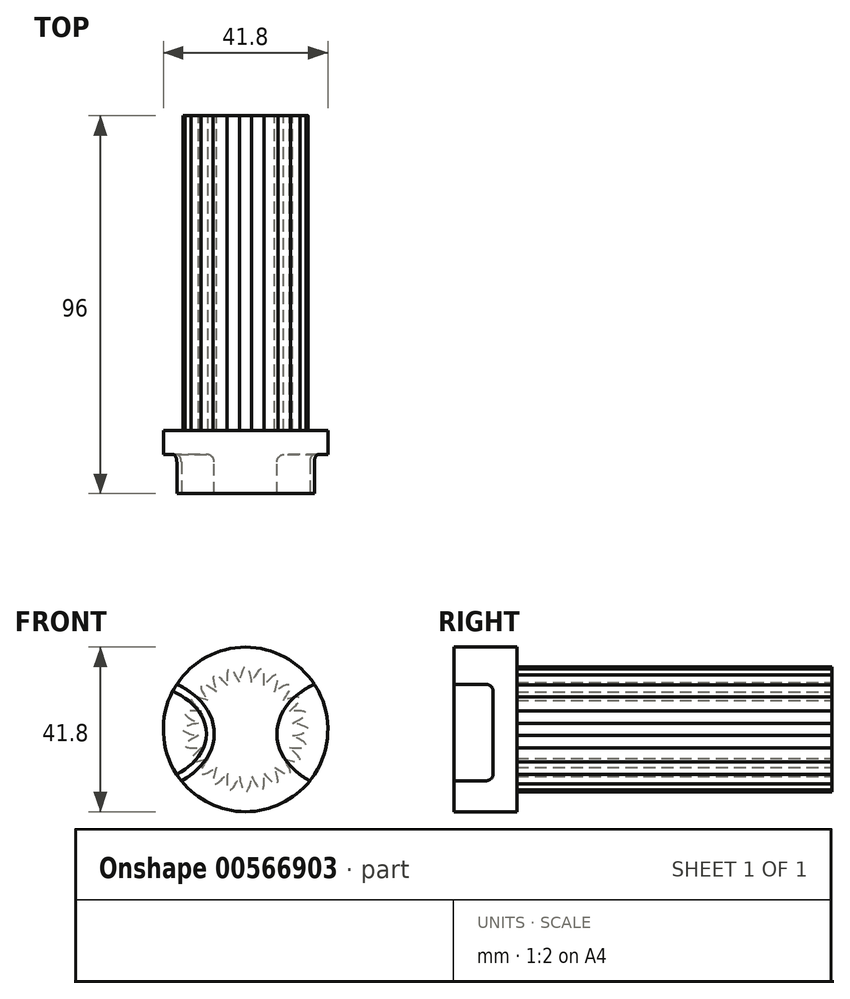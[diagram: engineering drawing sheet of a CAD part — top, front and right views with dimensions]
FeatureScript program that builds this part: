
annotation { "Feature Type Name" : "Feature", "Feature Type Description" : "" }
export const myFeature = defineFeature(function(context is Context, id is Id, definition is map)
    precondition{}
    {
        {
            var Q0;
            Q0=qCreatedBy(makeId("Front.planeOp"),FACE);
            var sketch = newSketch(context, id + "F0", { "sketchPlane" : qUnion([Q0])});
            skEllipse(sketch, "E0", {"center": v(0, 21) * mm, "majorRadius": 15.9 * mm, "minorRadius": 2.4 * mm, "majorAxis": v(0, -1)});
            skSolve(sketch);
        }
        {
            var Q0;
            Q0=makeQuery(id+"F0.imprint","IMPRINT",FACE,{"disambiguationData":[TD([[makeQuery(id+"F0.imprint","IMPRINT",EDGE,{"derivedFrom":sQuery(id+"F0.wireOp",EDGE,"E0")}),1.0]])]});
            extrude(context, id + "F1", {"entities" : qUnion([Q0]), "depth" : 96 * mm, "offsetDistance" : 25 * mm});
        }
        {
            var Q0;
            Q0=qCreatedBy(makeId("Right.planeOp"),FACE);
            var sketch = newSketch(context, id + "F2", { "sketchPlane" : qUnion([Q0])});
            skLineSegment(sketch, "E1", {"start": v(57.9, 21) * mm, "end": v(-81.94, 21) * mm});
            skSolve(sketch);
        }
        {
            var Q0;
            Q0=makeQuery(id+"F1.opExtrude","SWEPT_BODY",BODY,{"disambiguationData":[OSD([sQuery(id+"F0.wireOp",EDGE,"E0")])]});
            var Q1;
            Q1=sQuery(id+"F2.wireOp",EDGE,"E1");
            circularPattern(context, id + "F3", {"operationType" : NewBodyOperationType.ADD, "entities" : qUnion([Q0]), "axis" : qUnion([Q1]), "angle" : 360 * degree, "instanceCount" : 24, "equalSpace" : true});
        }
        {
            var Q0;
            {var subQ0=makeQuery(id+"F1.opExtrude","CAP_FACE",FACE,{"disambiguationData":[OSD([sQuery(id+"F0.wireOp",EDGE,"E0")])],"isStart":false});Q0=makeQuery(id+"F3.boolean.opBoolean","MERGE",FACE,{"derivedFrom":[subQ0,makeQuery(id+"F3.opPattern","COPY",FACE,{"derivedFrom":subQ0,"instanceName":"1"}),makeQuery(id+"F3.opPattern","COPY",FACE,{"derivedFrom":subQ0,"instanceName":"2"}),makeQuery(id+"F3.opPattern","COPY",FACE,{"derivedFrom":subQ0,"instanceName":"3"}),makeQuery(id+"F3.opPattern","COPY",FACE,{"derivedFrom":subQ0,"instanceName":"4"}),makeQuery(id+"F3.opPattern","COPY",FACE,{"derivedFrom":subQ0,"instanceName":"5"}),makeQuery(id+"F3.opPattern","COPY",FACE,{"derivedFrom":subQ0,"instanceName":"6"}),makeQuery(id+"F3.opPattern","COPY",FACE,{"derivedFrom":subQ0,"instanceName":"7"}),makeQuery(id+"F3.opPattern","COPY",FACE,{"derivedFrom":subQ0,"instanceName":"8"}),makeQuery(id+"F3.opPattern","COPY",FACE,{"derivedFrom":subQ0,"instanceName":"9"}),makeQuery(id+"F3.opPattern","COPY",FACE,{"derivedFrom":subQ0,"instanceName":"10"}),makeQuery(id+"F3.opPattern","COPY",FACE,{"derivedFrom":subQ0,"instanceName":"11"}),makeQuery(id+"F3.opPattern","COPY",FACE,{"derivedFrom":subQ0,"instanceName":"12"}),makeQuery(id+"F3.opPattern","COPY",FACE,{"derivedFrom":subQ0,"instanceName":"13"}),makeQuery(id+"F3.opPattern","COPY",FACE,{"derivedFrom":subQ0,"instanceName":"14"}),makeQuery(id+"F3.opPattern","COPY",FACE,{"derivedFrom":subQ0,"instanceName":"15"}),makeQuery(id+"F3.opPattern","COPY",FACE,{"derivedFrom":subQ0,"instanceName":"16"}),makeQuery(id+"F3.opPattern","COPY",FACE,{"derivedFrom":subQ0,"instanceName":"17"}),makeQuery(id+"F3.opPattern","COPY",FACE,{"derivedFrom":subQ0,"instanceName":"18"}),makeQuery(id+"F3.opPattern","COPY",FACE,{"derivedFrom":subQ0,"instanceName":"19"}),makeQuery(id+"F3.opPattern","COPY",FACE,{"derivedFrom":subQ0,"instanceName":"20"}),makeQuery(id+"F3.opPattern","COPY",FACE,{"derivedFrom":subQ0,"instanceName":"21"}),makeQuery(id+"F3.opPattern","COPY",FACE,{"derivedFrom":subQ0,"instanceName":"22"}),makeQuery(id+"F3.opPattern","COPY",FACE,{"derivedFrom":subQ0,"instanceName":"23"})]});}
            var sketch = newSketch(context, id + "F4", { "sketchPlane" : qUnion([Q0])});
            skCircle(sketch, "E2", {"center": v(0, 21) * mm, "radius": 20.9 * mm});
            skSolve(sketch);
        }
        {
            var Q0;
            Q0=makeQuery(id+"F4.imprint","IMPRINT",FACE,{"disambiguationData":[TD([[makeQuery(id+"F4.imprint","IMPRINT",EDGE,{"derivedFrom":sQuery(id+"F4.wireOp",EDGE,"E2")}),1.0]])]});
            extrude(context, id + "F5", {"entities" : qUnion([Q0]), "operationType" : NewBodyOperationType.ADD, "depth" : -16 * mm, "offsetDistance" : 25 * mm});
        }
        {
            var Q0;
            {var subQ0=sQuery(id+"F0.wireOp",EDGE,"E0");var subQ1=makeQuery(id+"F1.opExtrude","CAP_FACE",FACE,{"disambiguationData":[OSD([subQ0])],"isStart":false});Q0=makeQuery(id+"F5.boolean.opBoolean","MERGE",FACE,{"derivedFrom":[makeQuery(id+"F3.boolean.opBoolean","MERGE",FACE,{"derivedFrom":[subQ1,makeQuery(id+"F3.opPattern","COPY",FACE,{"derivedFrom":subQ1,"instanceName":"1"}),makeQuery(id+"F3.opPattern","COPY",FACE,{"derivedFrom":subQ1,"instanceName":"2"}),makeQuery(id+"F3.opPattern","COPY",FACE,{"derivedFrom":subQ1,"instanceName":"3"}),makeQuery(id+"F3.opPattern","COPY",FACE,{"derivedFrom":subQ1,"instanceName":"4"}),makeQuery(id+"F3.opPattern","COPY",FACE,{"derivedFrom":subQ1,"instanceName":"5"}),makeQuery(id+"F3.opPattern","COPY",FACE,{"derivedFrom":subQ1,"instanceName":"6"}),makeQuery(id+"F3.opPattern","COPY",FACE,{"derivedFrom":subQ1,"instanceName":"7"}),makeQuery(id+"F3.opPattern","COPY",FACE,{"derivedFrom":subQ1,"instanceName":"8"}),makeQuery(id+"F3.opPattern","COPY",FACE,{"derivedFrom":subQ1,"instanceName":"9"}),makeQuery(id+"F3.opPattern","COPY",FACE,{"derivedFrom":subQ1,"instanceName":"10"}),makeQuery(id+"F3.opPattern","COPY",FACE,{"derivedFrom":subQ1,"instanceName":"11"}),makeQuery(id+"F3.opPattern","COPY",FACE,{"derivedFrom":subQ1,"instanceName":"12"}),makeQuery(id+"F3.opPattern","COPY",FACE,{"derivedFrom":subQ1,"instanceName":"13"}),makeQuery(id+"F3.opPattern","COPY",FACE,{"derivedFrom":subQ1,"instanceName":"14"}),makeQuery(id+"F3.opPattern","COPY",FACE,{"derivedFrom":subQ1,"instanceName":"15"}),makeQuery(id+"F3.opPattern","COPY",FACE,{"derivedFrom":subQ1,"instanceName":"16"}),makeQuery(id+"F3.opPattern","COPY",FACE,{"derivedFrom":subQ1,"instanceName":"17"}),makeQuery(id+"F3.opPattern","COPY",FACE,{"derivedFrom":subQ1,"instanceName":"18"}),makeQuery(id+"F3.opPattern","COPY",FACE,{"derivedFrom":subQ1,"instanceName":"19"}),makeQuery(id+"F3.opPattern","COPY",FACE,{"derivedFrom":subQ1,"instanceName":"20"}),makeQuery(id+"F3.opPattern","COPY",FACE,{"derivedFrom":subQ1,"instanceName":"21"}),makeQuery(id+"F3.opPattern","COPY",FACE,{"derivedFrom":subQ1,"instanceName":"22"}),makeQuery(id+"F3.opPattern","COPY",FACE,{"derivedFrom":subQ1,"instanceName":"23"})]}),makeQuery(id+"F5.opExtrude","CAP_FACE",FACE,{"disambiguationData":[OSD([subQ0,sQuery(id+"F4.wireOp",EDGE,"E2")])],"isStart":true})]});}
            var sketch = newSketch(context, id + "F6", { "sketchPlane" : qUnion([Q0])});
            skEllipse(sketch, "E3", {"center": v(-28.96, 19.93) * mm, "majorRadius": 15 * mm, "minorRadius": 21 * mm, "majorAxis": v(0, 1)});
            skEllipse(sketch, "E4.MirrorC", {"center": v(28.96, 19.93) * mm, "majorRadius": 15 * mm, "minorRadius": 21 * mm, "majorAxis": v(0, 1)});
            skSolve(sketch);
        }
        {
            var Q0;
            Q0 = qSketchRegion(id + "F6", true);
            extrude(context, id + "F7", {"entities" : qUnion([Q0]), "operationType" : NewBodyOperationType.REMOVE, "oppositeDirection" : true, "depth" : 10 * mm, "offsetDistance" : 25 * mm});
        }
        {
            var Q0;
            Q0=makeQuery(id+"F7.boolean.opBoolean","COPY",EDGE,{"derivedFrom":makeQuery(id+"F7.opExtrude","CAP_EDGE",EDGE,{"disambiguationData":[OSD([sQuery(id+"F6.wireOp",EDGE,"E4.MirrorC")])],"isStart":false})});
            var Q1;
            Q1=makeQuery(id+"F7.boolean.opBoolean","COPY",EDGE,{"derivedFrom":makeQuery(id+"F7.opExtrude","CAP_EDGE",EDGE,{"disambiguationData":[OSD([sQuery(id+"F6.wireOp",EDGE,"E3")])],"isStart":false})});
            fillet(context, id + "F8", {"entities" : qUnion([Q0, Q1]), "radius" : 2 * mm, "tangentPropagation" : true, "allowEdgeOverflow" : false});
        }
    });
